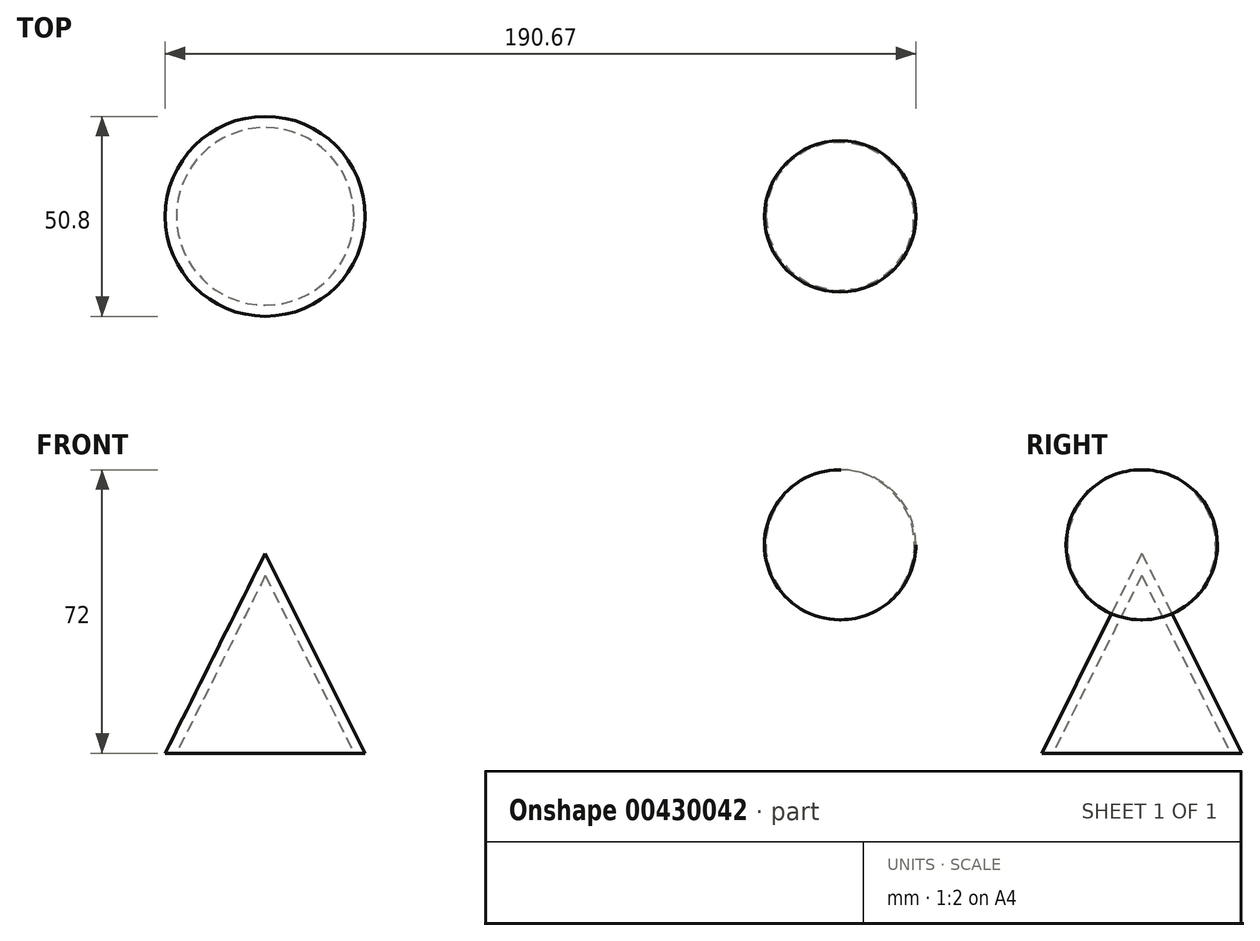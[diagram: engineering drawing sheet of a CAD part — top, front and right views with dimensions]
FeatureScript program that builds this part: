
annotation { "Feature Type Name" : "Feature", "Feature Type Description" : "" }
export const myFeature = defineFeature(function(context is Context, id is Id, definition is map)
    precondition{}
    {
        {
            var Q0;
            Q0=qCreatedBy(makeId("Front.planeOp"),FACE);
            var sketch = newSketch(context, id + "F0", { "sketchPlane" : qUnion([Q0])});
            skLineSegment(sketch, "E0", {"start": v(-40.23, 43.8) * mm, "end": v(-40.23, -7) * mm});
            skLineSegment(sketch, "E1", {"start": v(-40.23, 43.8) * mm, "end": v(-14.83, -7) * mm});
            skLineSegment(sketch, "E2", {"start": v(-14.83, -7) * mm, "end": v(-40.23, -7) * mm});
            skSolve(sketch);
        }
        {
            var Q0;
            Q0=makeQuery(id+"F0.imprint","IMPRINT",FACE,{"disambiguationData":[TD([[makeQuery(id+"F0.imprint","IMPRINT",EDGE,{"derivedFrom":sQuery(id+"F0.wireOp",EDGE,"E0")}),1.0]])]});
            var Q1;
            Q1=sQuery(id+"F0.wireOp",EDGE,"E0");
            revolve(context, id + "F1", {"entities" : qUnion([Q0]), "axis" : qUnion([Q1]), "revolveType" : RevolveType.FULL});
        }
        {
            var Q0;
            Q0=makeQuery(id+"F1.opRevolve","SWEPT_FACE",FACE,{"disambiguationData":[OSD([sQuery(id+"F0.wireOp",EDGE,"E2")])]});
            shell(context, id + "F2", {"entities" : qUnion([Q0]), "thickness" : 2.54 * mm});
        }
        {
            var Q0;
            Q0=qCreatedBy(makeId("Front.planeOp"),FACE);
            var sketch = newSketch(context, id + "F3", { "sketchPlane" : qUnion([Q0])});
            skCircle(sketch, "E3", {"center": v(106, 45.95) * mm, "radius": 19.05 * mm});
            skLineSegment(sketch, "E4", {"start": v(105.83, 65) * mm, "end": v(105.83, 26.9) * mm});
            skSolve(sketch);
        }
        {
            var Q0;
            {var subQ0=sQuery(id+"F3.wireOp",EDGE,"E4");Q0=makeQuery(id+"F3.imprint","IMPRINT",FACE,{"disambiguationData":[TD([[makeQuery(id+"F3.imprint","IMPRINT",EDGE,{"derivedFrom":subQ0}),-1.0]])]});}
            var Q1;
            Q1=sQuery(id+"F3.wireOp",EDGE,"E4");
            revolve(context, id + "F4", {"entities" : qUnion([Q0]), "axis" : qUnion([Q1]), "revolveType" : RevolveType.FULL});
        }
    });
